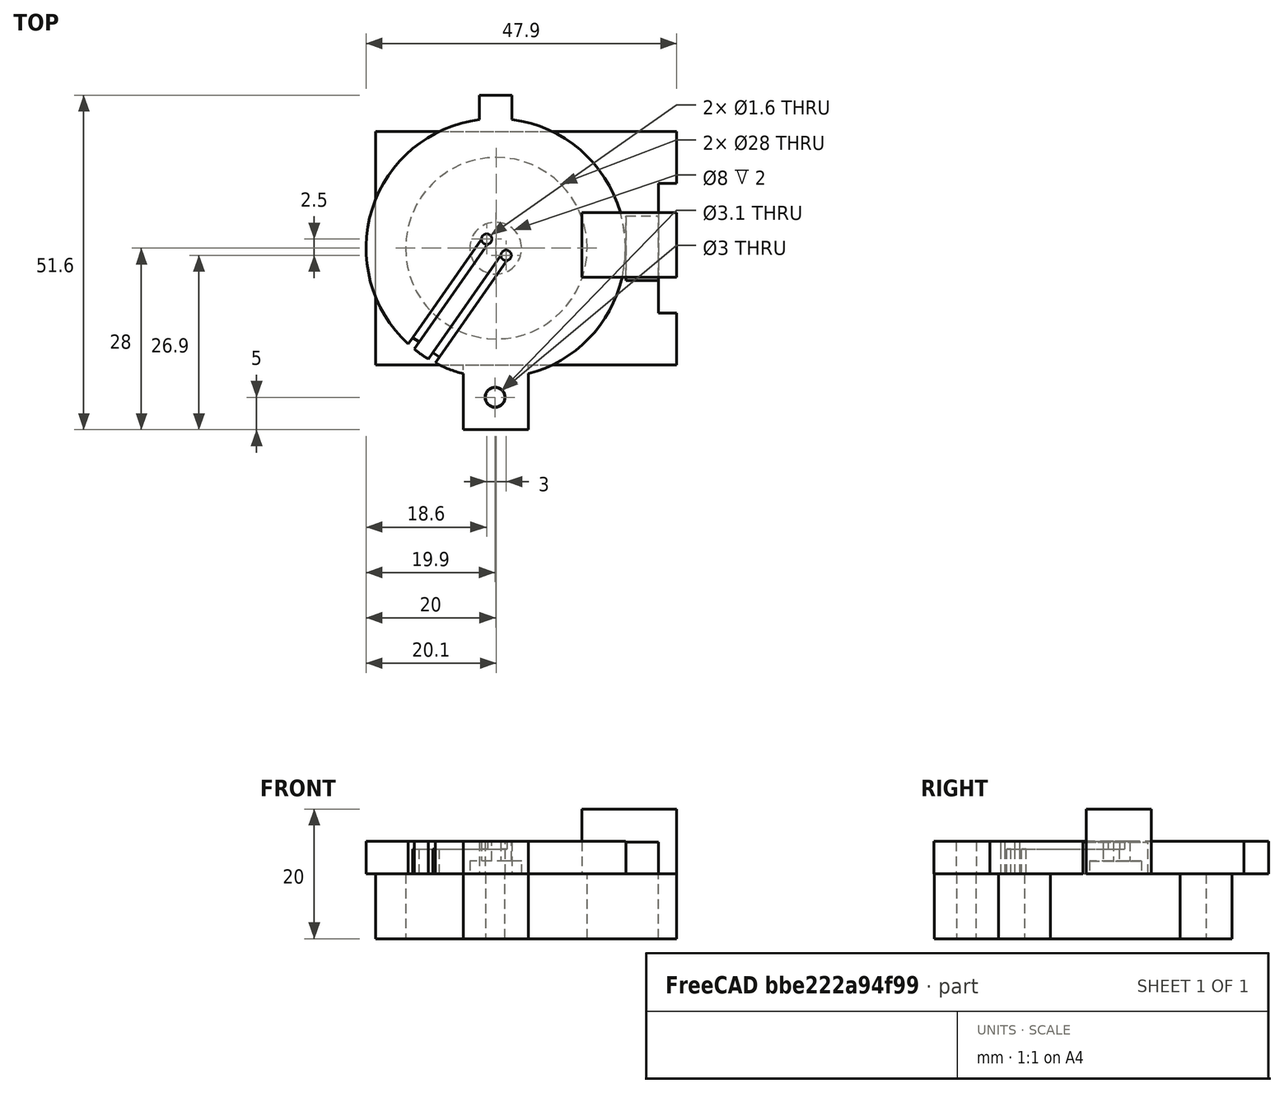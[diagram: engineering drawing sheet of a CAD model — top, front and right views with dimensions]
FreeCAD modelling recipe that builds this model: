
FCSTD DOCUMENT  (FreeCAD 1.0R39319 (Git))
Label: CdSHolderBooleaned2
License: All rights reserved
LicenseURL: https://en.wikipedia.org/wiki/All_rights_reserved
objects: Part::Box×11, Part::Cut×11, Part::Cylinder×7, Part::Fuse×5
note: 34 computed .brp shape members not serialized (recipe doc carries the construction recipe); baked Part::Feature solids carry a one-line shape summary decoded from their .brp

FEATURE [Part::Cylinder] Cylinder  label="cardboardBarrelHolder"
  Angle = 360
  AttacherType = Attacher::AttachEngine3D
  FirstAngle = 0
  Height = 40
  Placement = pos=(-1.1,0,-20) rot=(0,0,1;0rad)
  Radius = 14
  SecondAngle = 0
FEATURE [Part::Box] Box  label="mainPiece"
  AttacherType = Attacher::AttachEngine3D
  Height = 46.4
  Length = 10
  Placement = pos=(-19.7,-18,-4.4e-15) rot=(0,1,0;1.5708rad)
  Width = 36
FEATURE [Part::Box] Box001  label="Cube001"
  AttacherType = Attacher::AttachEngine3D
  Height = 14.6
  Length = 10
  Placement = pos=(12.1,-4.5,10) rot=(0,1,0;1.5708rad)
  Width = 10
FEATURE [Part::Box] Box002  label="hingePinTab"
  AttacherType = Attacher::AttachEngine3D
  Height = 10
  Length = 10
  Placement = pos=(-6.2,-27.952,-10) rot=(0,0,1;0rad)
  Width = 10
FEATURE [Part::Cylinder] Cylinder001  label="hingeTabHole"
  Angle = 360
  AttacherType = Attacher::AttachEngine3D
  FirstAngle = 0
  Height = 30
  Placement = pos=(-1.3,-23,-12) rot=(0,0,1;0rad)
  Radius = 1.5
  SecondAngle = 0
FEATURE [Part::Cylinder] Cylinder002  label="shutter"
  Angle = 360
  AttacherType = Attacher::AttachEngine3D
  FirstAngle = 0
  Height = 5
  Placement = pos=(-1.2,0,0) rot=(0,0,1;0rad)
  Radius = 20
  SecondAngle = 0
FEATURE [Part::Box] Box003  label="shutterHingeTab"
  AttacherType = Attacher::AttachEngine3D
  Height = 5
  Length = 10
  Placement = pos=(-6.2,-28,0) rot=(0,0,1;0rad)
  Width = 14
FEATURE [Part::Box] Box004  label="swivelStop"
  AttacherType = Attacher::AttachEngine3D
  Height = 5
  Length = 5
  Placement = pos=(18.9,-5,-0.1) rot=(0,0,1;0rad)
  Width = 10
FEATURE [Part::Box] Box005  label="footCutout"
  AttacherType = Attacher::AttachEngine3D
  Height = 20
  Length = 10
  Placement = pos=(23.9,-10,-18) rot=(0,0,1;0rad)
  Width = 20
FEATURE [Part::Cylinder] Cylinder003  label="shutterTabHole"
  Angle = 360
  AttacherType = Attacher::AttachEngine3D
  FirstAngle = 0
  Height = 50
  Placement = pos=(-1.3,-23,-12) rot=(0,0,1;0rad)
  Radius = 1.55
  SecondAngle = 0
FEATURE [Part::Box] Box006  label="shutterMoveTab"
  AttacherType = Attacher::AttachEngine3D
  Height = 5
  Length = 5
  Placement = pos=(-3.7,18.6,0) rot=(0,0,1;0rad)
  Width = 5
FEATURE [Part::Cylinder] Cylinder004  label="CdSDivot"
  Angle = 360
  AttacherType = Attacher::AttachEngine3D
  FirstAngle = 0
  Height = 10
  Placement = pos=(-1.2,0,-8) rot=(0,0,1;0rad)
  Radius = 4
  SecondAngle = 0
FEATURE [Part::Cylinder] Cylinder005  label="CdSWire1"
  Angle = 360
  AttacherType = Attacher::AttachEngine3D
  FirstAngle = 0
  Height = 30
  Placement = pos=(0.4,-1.1,-18) rot=(0,0,1;0rad)
  Radius = 0.8
  SecondAngle = 0
FEATURE [Part::Cylinder] Cylinder006  label="CdsWire2"
  Angle = 360
  AttacherType = Attacher::AttachEngine3D
  FirstAngle = 0
  Height = 30
  Placement = pos=(-2.6,1.4,-18) rot=(0,0,1;0rad)
  Radius = 0.8
  SecondAngle = 0
FEATURE [Part::Box] Box007  label="radialTransit1"
  AttacherType = Attacher::AttachEngine3D
  Height = 10
  Length = 1.2
  Placement = pos=(-17.353,-25.3595,3.8) rot=(0,0,1;5.67232rad)
  Width = 30
FEATURE [Part::Box] Box008  label="radialTransit2"
  AttacherType = Attacher::AttachEngine3D
  Height = 10
  Length = 1.2
  Placement = pos=(-20.3756,-22.8768,3.8) rot=(0,0,1;5.67232rad)
  Width = 30
FEATURE [Part::Box] Box009  label="radialTransit3"
  AttacherType = Attacher::AttachEngine3D
  Height = 10
  Length = 1.2
  Placement = pos=(-10.8716,-16.103,-4.1) rot=(-0.913318,0.287968,0.287968;4.62184rad)
  Width = 30
FEATURE [Part::Box] Box010  label="radialTransit4"
  AttacherType = Attacher::AttachEngine3D
  Height = 10
  Length = 1.2
  Placement = pos=(-14.0089,-13.7842,-4.1) rot=(-0.913318,0.287968,0.287968;4.62184rad)
  Width = 30
FEATURE [Part::Cut] Cut
  Base = -> Box
  Tool = -> Cylinder
FEATURE [Part::Cut] Cut001  label="mainPiece1"
  Base = -> Cut
  Tool = -> Box005
FEATURE [Part::Cut] Cut002
  Base = -> Cylinder002
  Tool = -> Cylinder004
FEATURE [Part::Cut] Cut003
  Base = -> Cut002
  Tool = -> Cylinder005
FEATURE [Part::Cut] Cut004
  Base = -> Cut003
  Tool = -> Cylinder006
FEATURE [Part::Cut] Cut005
  Base = -> Cut004
  Tool = -> Box007
FEATURE [Part::Cut] Cut006
  Base = -> Cut005
  Tool = -> Box008
FEATURE [Part::Cut] Cut007
  Base = -> Cut006
  Tool = -> Box009
FEATURE [Part::Cut] Cut008  label="shutter1"
  Base = -> Cut007
  Tool = -> Box010
FEATURE [Part::Cut] Cut009  label="shutterHingeTab001"
  Base = -> Box003
  Tool = -> Cylinder003
FEATURE [Part::Cut] Cut010  label="mainPieceHingeTab"
  Base = -> Box002
  Tool = -> Cylinder001
FEATURE [Part::Fuse] Fusion  label="mainPiece2"
  Base = -> Cut001
  Tool = -> Cut010
FEATURE [Part::Fuse] Fusion001  label="shutter2"
  Base = -> Cut008
  Tool = -> Cut009
FEATURE [Part::Fuse] Fusion002  label="Don'tUsemainPiece3"
  Base = -> Cut001
  Tool = -> Box004
FEATURE [Part::Fuse] Fusion003  label="shutter4"
  Base = -> Fusion001
  Tool = -> Box006
FEATURE [Part::Fuse] Fusion004  label="mainPiece10"
  Base = -> Fusion
  Tool = -> Box004
